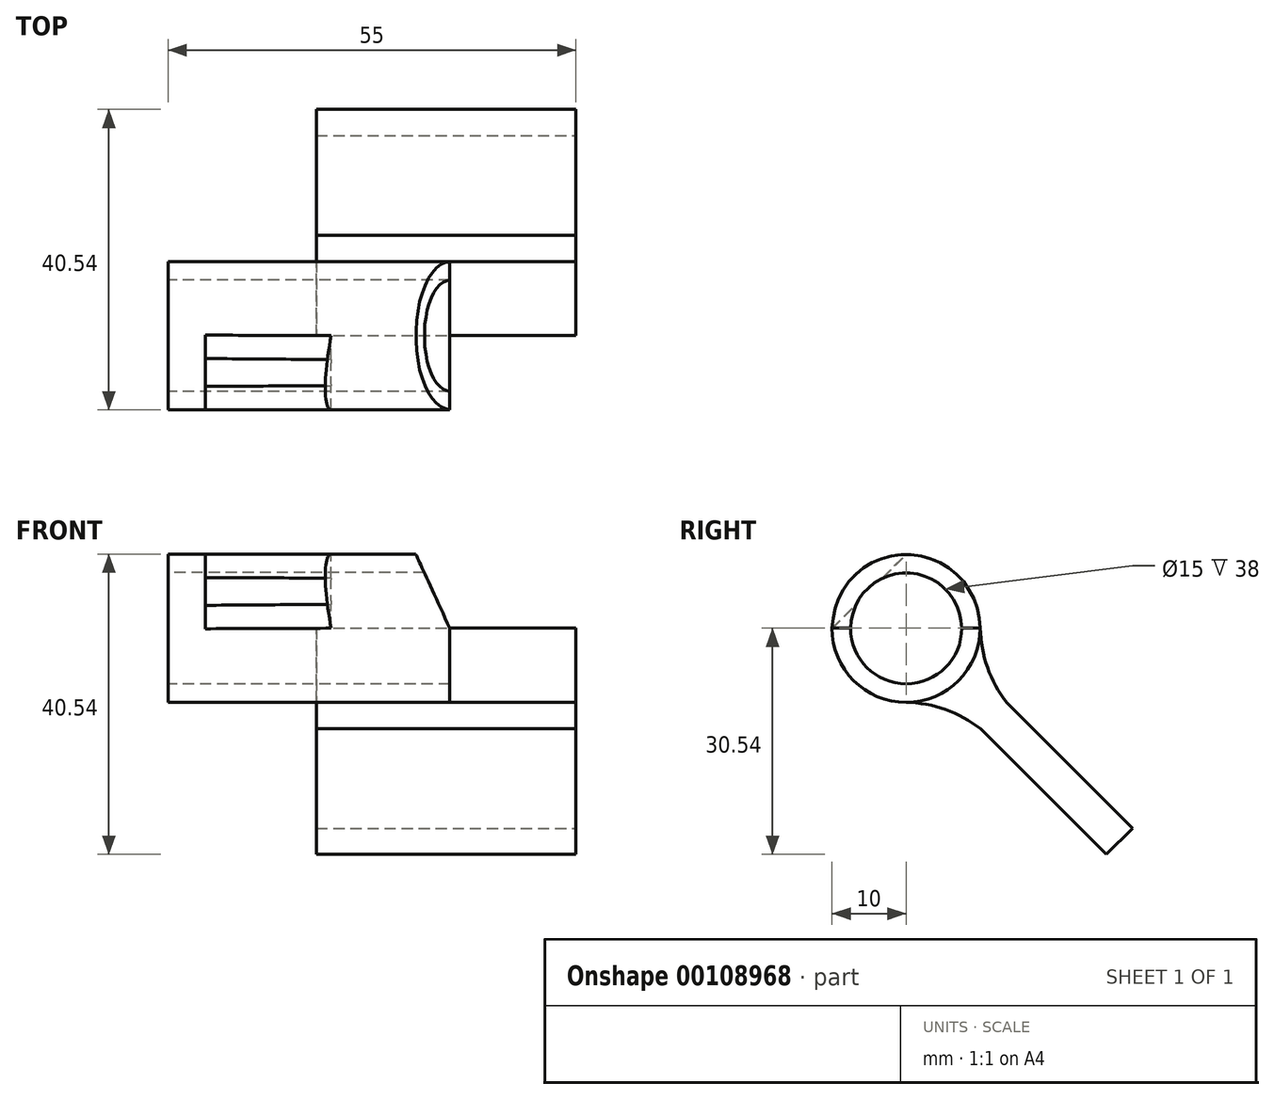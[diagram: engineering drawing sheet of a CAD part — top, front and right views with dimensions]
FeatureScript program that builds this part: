
annotation { "Feature Type Name" : "Feature", "Feature Type Description" : "" }
export const myFeature = defineFeature(function(context is Context, id is Id, definition is map)
    precondition{}
    {
        {
            var Q0;
            Q0=qCreatedBy(makeId("Right.planeOp"),FACE);
            var sketch = newSketch(context, id + "F0", { "sketchPlane" : qUnion([Q0])});
            skCircle(sketch, "E0", {"center": v(0, 0) * mm, "radius": 7.5 * mm});
            skCircle(sketch, "E1", {"center": v(0, 0) * mm, "radius": 10 * mm});
            skLineSegment(sketch, "E2", {"start": v(0, 0) * mm, "end": v(28.28, -28.28) * mm, "construction": true});
            skArc(sketch, "E3", {"start": v(10, 0) * mm, "mid": v(10.98, -5.3) * mm, "end": v(13.57, -10.04) * mm});
            skLineSegment(sketch, "E4", {"start": v(13.57, -10.04) * mm, "end": v(10.04, -13.57) * mm, "construction": true});
            skArc(sketch, "E5", {"start": v(10.04, -13.57) * mm, "mid": v(5.3, -10.98) * mm, "end": v(0, -10) * mm});
            skLineSegment(sketch, "E6", {"start": v(27, -30.54) * mm, "end": v(30.54, -27) * mm});
            skLineSegment(sketch, "E7", {"start": v(10.04, -13.57) * mm, "end": v(27, -30.54) * mm});
            skLineSegment(sketch, "E8", {"start": v(13.57, -10.04) * mm, "end": v(30.54, -27) * mm});
            skSolve(sketch);
        }
        {
            var Q0;
            Q0=makeQuery(id+"F0.imprint","IMPRINT",FACE,{"disambiguationData":[TD([[makeQuery(id+"F0.imprint","IMPRINT",EDGE,{"derivedFrom":sQuery(id+"F0.wireOp",EDGE,"E0")}),-1.0]])]});
            extrude(context, id + "F1", {"entities" : qUnion([Q0]), "depth" : 8 * mm});
        }
        {
            var Q0;
            Q0=makeQuery(id+"F0.imprint","IMPRINT",FACE,{"disambiguationData":[TD([[makeQuery(id+"F0.imprint","IMPRINT",EDGE,{"derivedFrom":sQuery(id+"F0.wireOp",EDGE,"E0")}),-1.0]])]});
            extrude(context, id + "F2", {"entities" : qUnion([Q0]), "operationType" : NewBodyOperationType.ADD, "depth" : 5 * mm, "hasSecondDirection" : true, "secondDirectionOppositeDirection" : true, "secondDirectionDepth" : 30 * mm});
        }
        {
            var Q0;
            Q0=qCreatedBy(makeId("Front.planeOp"),FACE);
            var sketch = newSketch(context, id + "F3", { "sketchPlane" : qUnion([Q0])});
            skLineSegment(sketch, "E9.0", {"start": v(8, 10) * mm, "end": v(8, 0) * mm});
            skLineSegment(sketch, "E10", {"start": v(-30, 10) * mm, "end": v(3.42, 10) * mm});
            skLineSegment(sketch, "E11", {"start": v(8, 0) * mm, "end": v(3.42, 10) * mm});
            skLineSegment(sketch, "E12", {"start": v(3.42, 10) * mm, "end": v(8, 10) * mm});
            skLineSegment(sketch, "E13", {"start": v(8, 0) * mm, "end": v(8, -10) * mm});
            skSolve(sketch);
        }
        {
            var Q0;
            Q0=makeQuery(id+"F3.imprint","IMPRINT",FACE,{"disambiguationData":[TD([[makeQuery(id+"F3.imprint","IMPRINT",EDGE,{"derivedFrom":sQuery(id+"F3.wireOp",EDGE,"E9.0")}),-1.0]])]});
            extrude(context, id + "F4", {"entities" : qUnion([Q0]), "operationType" : NewBodyOperationType.REMOVE, "depth" : 25 * mm, "symmetric" : true});
        }
        {
            var Q0;
            {var subQ1=sQuery(id+"F0.wireOp",EDGE,"E3");Q0=makeQuery(id+"F0.imprint","IMPRINT",FACE,{"disambiguationData":[TD([[makeQuery(id+"F0.imprint","IMPRINT",EDGE,{"derivedFrom":subQ1}),-1.0]])]});}
            extrude(context, id + "F5", {"entities" : qUnion([Q0]), "operationType" : NewBodyOperationType.ADD, "oppositeDirection" : true, "depth" : 10 * mm, "hasSecondDirection" : true, "secondDirectionOppositeDirection" : false, "secondDirectionDepth" : 25 * mm});
        }
        {
            var Q0;
            Q0=makeQuery(id+"F5.opExtrude","SWEPT_FACE",FACE,{"disambiguationData":[OSD([sQuery(id+"F0.wireOp",EDGE,"E8")])]});
            var sketch = newSketch(context, id + "F6", { "sketchPlane" : qUnion([Q0])});
            skPoint(sketch, "E14.0", {"position": v(8, 7.07) * mm});
            skArc(sketch, "E15", {"start": v(25, 40.7) * mm, "mid": v(14.67, 24.8) * mm, "end": v(8, 7.07) * mm});
            skLineSegment(sketch, "E16.0", {"start": v(-10, 7.07) * mm, "end": v(-10, 16.7) * mm, "construction": true});
            skLineSegment(sketch, "E17", {"start": v(-30, 10) * mm, "end": v(-10, 10) * mm, "construction": true});
            skArc(sketch, "E18", {"start": v(16.79, 40.7) * mm, "mid": v(3.3, 25.43) * mm, "end": v(-10, 10) * mm});
            skLineSegment(sketch, "E19", {"start": v(16.79, 40.7) * mm, "end": v(25, 40.7) * mm});
            skLineSegment(sketch, "E20", {"start": v(-10, 10) * mm, "end": v(8, 10) * mm});
            skLineSegment(sketch, "E21", {"start": v(8, 10) * mm, "end": v(8, 7.07) * mm});
            skLineSegment(sketch, "E22", {"start": v(-10, 10) * mm, "end": v(-10, 40.7) * mm});
            skLineSegment(sketch, "E23", {"start": v(-10, 40.7) * mm, "end": v(25, 40.7) * mm});
            skLineSegment(sketch, "E24", {"start": v(25, 40.7) * mm, "end": v(25, 7.02) * mm});
            skLineSegment(sketch, "E25", {"start": v(25, 7.02) * mm, "end": v(8, 7.07) * mm});
            skLineSegment(sketch, "E26", {"start": v(8, 7.07) * mm, "end": v(-10, 7.07) * mm});
            skLineSegment(sketch, "E27", {"start": v(-10, 7.07) * mm, "end": v(-10, 16.7) * mm});
            skSolve(sketch);
        }
        {
            var Q0;
            {var subQ0=sQuery(id+"F6.wireOp",EDGE,"E27");var subQ1=sQuery(id+"F6.wireOp",EDGE,"E18");var subQ2=makeQuery(id+"F6.imprint","INTERSECT",VERTEX,{"derivedFrom":[subQ1,sQuery(id+"F6.wireOp",EDGE,"E20"),subQ0]});Q0=makeQuery(id+"F6.imprint","IMPRINT",FACE,{"disambiguationData":[TD([[makeQuery(id+"F6.imprint","IMPRINT",EDGE,{"disambiguationData":[TD([[subQ2,1.0]])],"derivedFrom":subQ1}),-1.0]])]});}
            var Q1;
            {var subQ5=sQuery(id+"F6.wireOp",EDGE,"E22");Q1=makeQuery(id+"F6.imprint","IMPRINT",FACE,{"disambiguationData":[TD([[makeQuery(id+"F6.imprint","IMPRINT",EDGE,{"derivedFrom":subQ5}),-1.0]])]});}
            var Q2;
            {var subQ0=sQuery(id+"F6.wireOp",EDGE,"E24");var subQ1=sQuery(id+"F6.wireOp",EDGE,"E15");var subQ2=makeQuery(id+"F6.imprint","INTERSECT",VERTEX,{"derivedFrom":[subQ1,sQuery(id+"F6.wireOp",EDGE,"E23"),subQ0]});Q2=makeQuery(id+"F6.imprint","IMPRINT",FACE,{"disambiguationData":[TD([[makeQuery(id+"F6.imprint","IMPRINT",EDGE,{"disambiguationData":[TD([[subQ2,-1.0]])],"derivedFrom":subQ1}),1.0]])]});}
            var Q3;
            {var subQ0=sQuery(id+"F6.wireOp",EDGE,"E25");Q3=makeQuery(id+"F6.imprint","IMPRINT",FACE,{"disambiguationData":[TD([[makeQuery(id+"F6.imprint","IMPRINT",EDGE,{"derivedFrom":subQ0}),-1.0]])]});}
            extrude(context, id + "F7", {"entities" : qUnion([Q0, Q1, Q2, Q3]), "operationType" : NewBodyOperationType.REMOVE, "oppositeDirection" : true, "depth" : 25 * mm, "hasSecondDirection" : true, "secondDirectionOppositeDirection" : false, "secondDirectionDepth" : 25 * mm});
        }
    });
